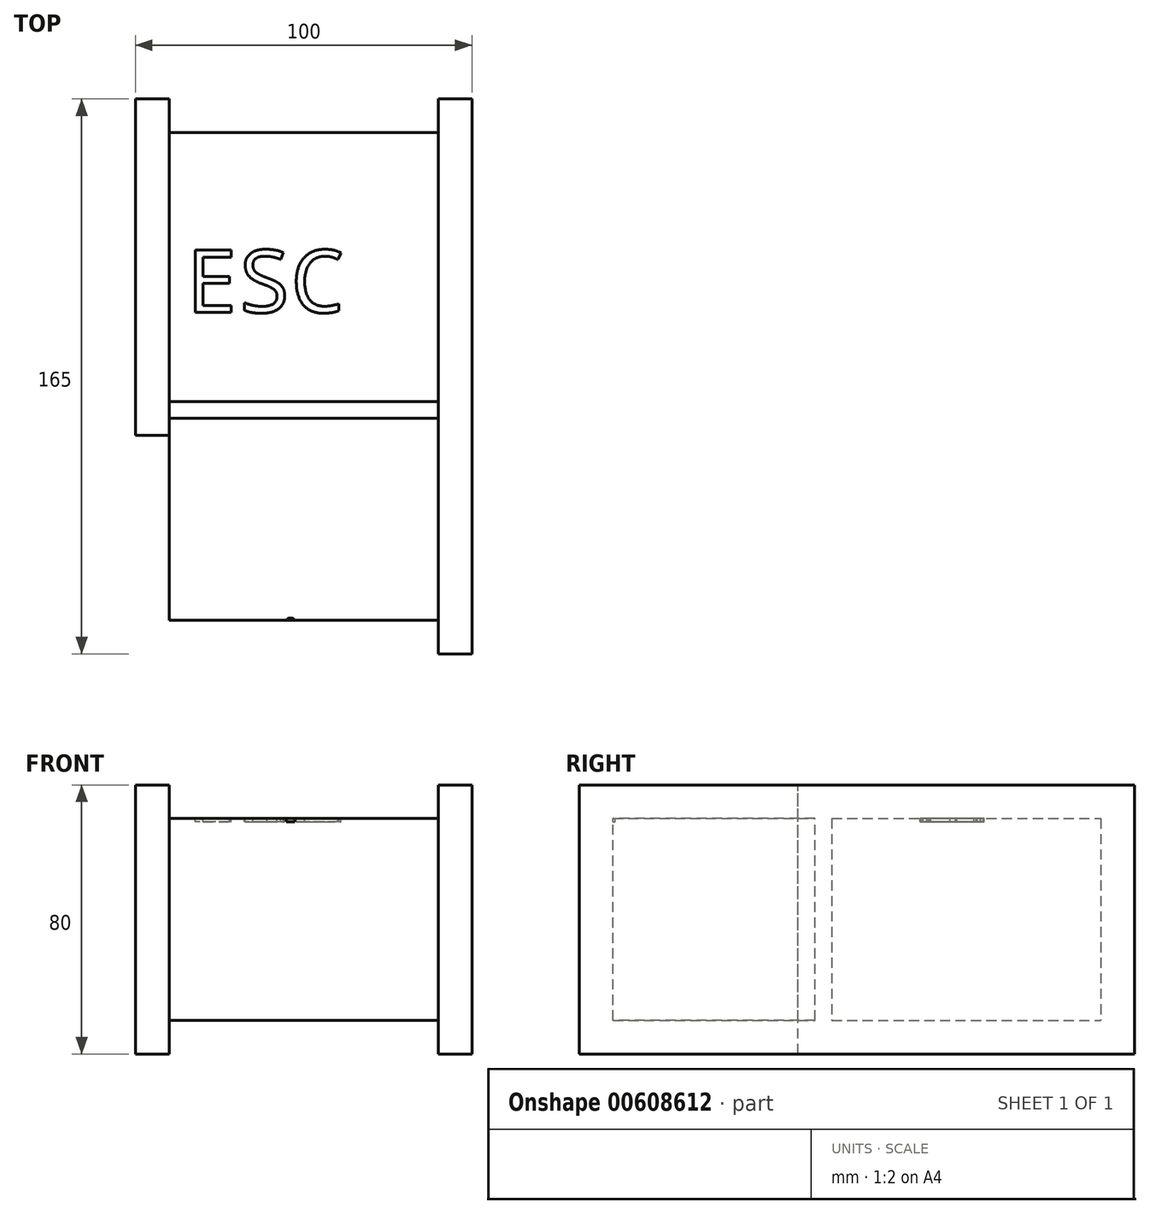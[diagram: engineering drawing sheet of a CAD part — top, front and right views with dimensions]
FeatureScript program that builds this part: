
annotation { "Feature Type Name" : "Feature", "Feature Type Description" : "" }
export const myFeature = defineFeature(function(context is Context, id is Id, definition is map)
    precondition{}
    {
        {
            var Q0;
            Q0=qCreatedBy(makeId("Right.planeOp"),FACE);
            var sketch = newSketch(context, id + "F0", { "sketchPlane" : qUnion([Q0])});
            skLineSegment(sketch, "E0.bottom", {"start": v(0, 0) * mm, "end": v(100, 0) * mm});
            skLineSegment(sketch, "E0.top", {"start": v(0, 80) * mm, "end": v(100, 80) * mm});
            skLineSegment(sketch, "E0.left", {"start": v(0, 0) * mm, "end": v(0, 80) * mm});
            skLineSegment(sketch, "E0.right", {"start": v(100, 0) * mm, "end": v(100, 80) * mm});
            skSolve(sketch);
        }
        {
            var Q0;
            Q0=makeQuery(id+"F0.imprint","IMPRINT",FACE,{"disambiguationData":[TD([[makeQuery(id+"F0.imprint","IMPRINT",EDGE,{"derivedFrom":sQuery(id+"F0.wireOp",EDGE,"E0.bottom")}),1.0]])]});
            extrude(context, id + "F1", {"entities" : qUnion([Q0]), "depth" : 10 * mm, "offsetDistance" : 25 * mm});
        }
        {
            var Q0;
            Q0=makeQuery(id+"F1.opExtrude","CAP_FACE",FACE,{"disambiguationData":[OSD([sQuery(id+"F0.wireOp",EDGE,"E0.bottom"),sQuery(id+"F0.wireOp",EDGE,"E0.top"),sQuery(id+"F0.wireOp",EDGE,"E0.left"),sQuery(id+"F0.wireOp",EDGE,"E0.right")])],"isStart":false});
            var sketch = newSketch(context, id + "F2", { "sketchPlane" : qUnion([Q0])});
            skLineSegment(sketch, "E1.bottom", {"start": v(10, 70) * mm, "end": v(90, 70) * mm});
            skLineSegment(sketch, "E1.top", {"start": v(10, 10) * mm, "end": v(90, 10) * mm});
            skLineSegment(sketch, "E1.left", {"start": v(10, 70) * mm, "end": v(10, 10) * mm});
            skLineSegment(sketch, "E1.right", {"start": v(90, 70) * mm, "end": v(90, 10) * mm});
            skSolve(sketch);
        }
        {
            var Q0;
            Q0=makeQuery(id+"F2.imprint","IMPRINT",FACE,{"disambiguationData":[TD([[makeQuery(id+"F2.imprint","IMPRINT",EDGE,{"derivedFrom":sQuery(id+"F2.wireOp",EDGE,"E1.bottom")}),-1.0]])]});
            extrude(context, id + "F3", {"entities" : qUnion([Q0]), "operationType" : NewBodyOperationType.ADD, "depth" : 80 * mm, "offsetDistance" : 25 * mm});
        }
        {
            var Q0;
            Q0=makeQuery(id+"F3.opExtrude","SWEPT_FACE",FACE,{"disambiguationData":[OSD([sQuery(id+"F2.wireOp",EDGE,"E1.bottom")])]});
            var sketch = newSketch(context, id + "F4", { "sketchPlane" : qUnion([Q0])});
            skText(sketch, "E2", { "text": "ESC", "fontName": "DroidSansMono.ttf"});
            const initialGuessF4  = {"E2": [0.015, 0.03653, 1, 0, 0.01869]};
            skSetInitialGuess(sketch, initialGuessF4);
            skSolve(sketch);
        }
        {
            var Q0;
            Q0 = qSketchRegion(id + "F4", true);
            extrude(context, id + "F5", {"entities" : qUnion([Q0]), "operationType" : NewBodyOperationType.REMOVE, "oppositeDirection" : true, "depth" : 1 * mm, "offsetDistance" : 25 * mm});
        }
        {
            var Q0;
            Q0=makeQuery(id+"F3.opExtrude","CAP_FACE",FACE,{"disambiguationData":[OSD([sQuery(id+"F2.wireOp",EDGE,"E1.bottom"),sQuery(id+"F2.wireOp",EDGE,"E1.top"),sQuery(id+"F2.wireOp",EDGE,"E1.left"),sQuery(id+"F2.wireOp",EDGE,"E1.right")])],"isStart":false});
            var sketch = newSketch(context, id + "F6", { "sketchPlane" : qUnion([Q0])});
            skLineSegment(sketch, "E3.bottom", {"start": v(100, 80) * mm, "end": v(-65, 80) * mm});
            skLineSegment(sketch, "E3.top", {"start": v(100, 0) * mm, "end": v(-65, 0) * mm});
            skLineSegment(sketch, "E3.left", {"start": v(100, 80) * mm, "end": v(100, 0) * mm});
            skLineSegment(sketch, "E3.right", {"start": v(-65, 80) * mm, "end": v(-65, 0) * mm});
            skSolve(sketch);
        }
        {
            var Q0;
            Q0 = qSketchRegion(id + "F6", true);
            var Q1;
            Q1=makeQuery(id+"F6.imprint","IMPRINT",FACE,{"disambiguationData":[TD([[makeQuery(id+"F6.imprint","IMPRINT",EDGE,{"derivedFrom":sQuery(id+"F6.wireOp",EDGE,"E3.bottom")}),1.0]])]});
            extrude(context, id + "F7", {"entities" : qUnion([Q0, Q1]), "operationType" : NewBodyOperationType.ADD, "depth" : 10 * mm, "offsetDistance" : 25 * mm});
        }
        {
            var Q0;
            Q0=makeQuery(id+"F7.opExtrude","CAP_FACE",FACE,{"disambiguationData":[OSD([sQuery(id+"F6.wireOp",EDGE,"E3.bottom"),sQuery(id+"F6.wireOp",EDGE,"E3.top"),sQuery(id+"F6.wireOp",EDGE,"E3.left"),sQuery(id+"F6.wireOp",EDGE,"E3.right")])],"isStart":true});
            var sketch = newSketch(context, id + "F8", { "sketchPlane" : qUnion([Q0])});
            skLineSegment(sketch, "E4.bottom", {"start": v(-5, 70) * mm, "end": v(55, 70) * mm});
            skLineSegment(sketch, "E4.top", {"start": v(-5, 10) * mm, "end": v(55, 10) * mm});
            skLineSegment(sketch, "E4.left", {"start": v(-5, 70) * mm, "end": v(-5, 10) * mm});
            skLineSegment(sketch, "E4.right", {"start": v(55, 70) * mm, "end": v(55, 10) * mm});
            skSolve(sketch);
        }
        {
            var Q0;
            Q0=makeQuery(id+"F8.imprint","IMPRINT",FACE,{"disambiguationData":[TD([[makeQuery(id+"F8.imprint","IMPRINT",EDGE,{"derivedFrom":sQuery(id+"F8.wireOp",EDGE,"E4.bottom")}),-1.0]])]});
            var Q1;
            Q1=makeQuery(id+"F1.opExtrude","CAP_FACE",FACE,{"disambiguationData":[OSD([sQuery(id+"F0.wireOp",EDGE,"E0.bottom"),sQuery(id+"F0.wireOp",EDGE,"E0.top"),sQuery(id+"F0.wireOp",EDGE,"E0.left"),sQuery(id+"F0.wireOp",EDGE,"E0.right")])],"isStart":false});
            extrude(context, id + "F9", {"entities" : qUnion([Q0]), "operationType" : NewBodyOperationType.ADD, "endBound" : BoundingType.UP_TO_SURFACE, "depth" : 25 * mm, "endBoundEntityFace" : qUnion([Q1]), "offsetDistance" : 25 * mm});
        }
        {
            var Q0;
            Q0=makeQuery(id+"F9.opExtrude","SWEPT_FACE",FACE,{"disambiguationData":[OSD([sQuery(id+"F8.wireOp",EDGE,"E4.bottom")])]});
            var sketch = newSketch(context, id + "F10", { "sketchPlane" : qUnion([Q0])});
            skText(sketch, "E5", { "text": "Reciever", "fontName": "OpenSans-Bold.ttf"});
            const initialGuessF10  = {"E5": [0.015, -0.06667, 1, 0, 0.01167]};
            skSetInitialGuess(sketch, initialGuessF10);
            skSolve(sketch);
        }
        {
            var Q0;
            Q0 = qSketchRegion(id + "F10", true);
            extrude(context, id + "F11", {"entities" : qUnion([Q0]), "operationType" : NewBodyOperationType.REMOVE, "oppositeDirection" : true, "depth" : 1 * mm, "offsetDistance" : 25 * mm});
        }
    });
